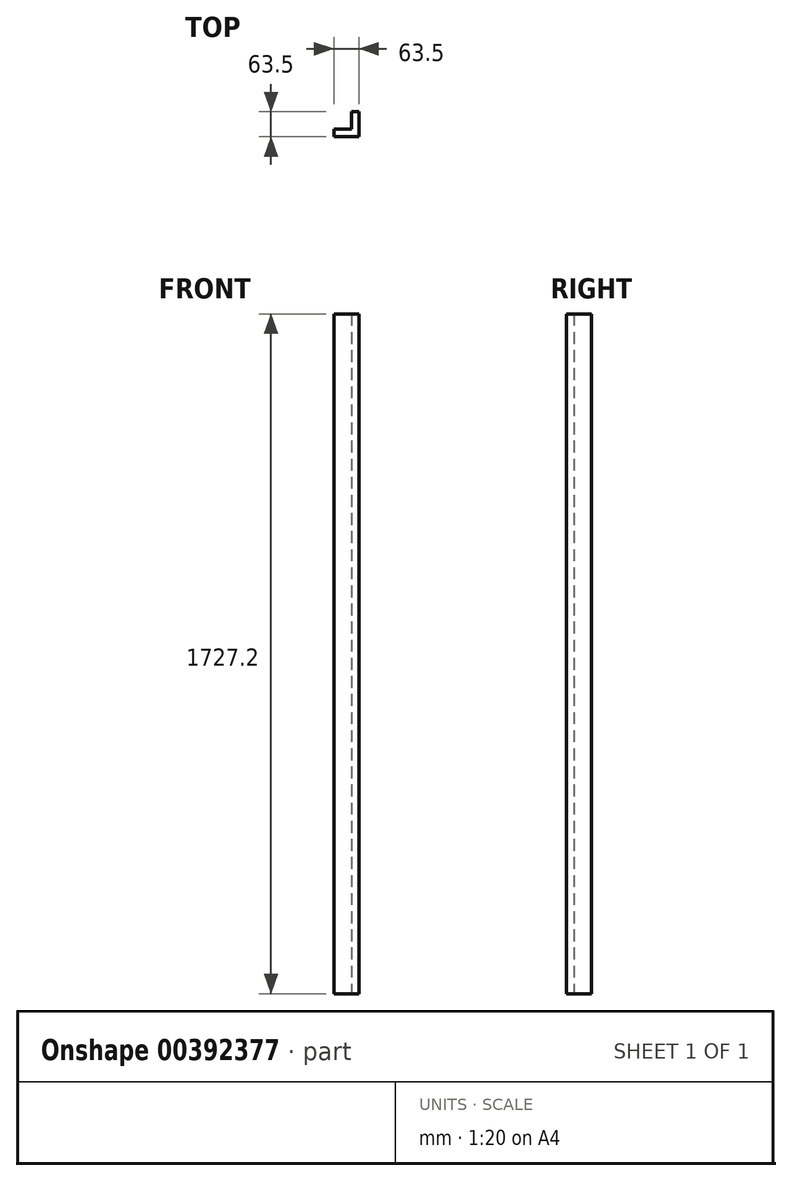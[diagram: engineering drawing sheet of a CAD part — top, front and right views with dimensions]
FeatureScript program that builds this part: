
annotation { "Feature Type Name" : "Feature", "Feature Type Description" : "" }
export const myFeature = defineFeature(function(context is Context, id is Id, definition is map)
    precondition{}
    {
        {
            var Q0;
            Q0=qCreatedBy(makeId("Top.planeOp"),FACE);
            var sketch = newSketch(context, id + "F0", { "sketchPlane" : qUnion([Q0])});
            skLineSegment(sketch, "E0", {"start": v(0, 0) * mm, "end": v(0, -63.5) * mm});
            skLineSegment(sketch, "E1", {"start": v(0, -63.5) * mm, "end": v(-63.5, -63.5) * mm});
            skLineSegment(sketch, "E2", {"start": v(-63.5, -63.5) * mm, "end": v(-63.5, -44.45) * mm});
            skLineSegment(sketch, "E3", {"start": v(-63.5, -44.45) * mm, "end": v(-19.05, -44.45) * mm});
            skLineSegment(sketch, "E4", {"start": v(-19.05, -44.45) * mm, "end": v(-19.05, 0) * mm});
            skLineSegment(sketch, "E5", {"start": v(-19.05, 0) * mm, "end": v(0, 0) * mm});
            skSolve(sketch);
        }
        {
            var Q0;
            Q0=makeQuery(id+"F0.imprint","IMPRINT",FACE,{"disambiguationData":[TD([[makeQuery(id+"F0.imprint","IMPRINT",EDGE,{"derivedFrom":sQuery(id+"F0.wireOp",EDGE,"E0")}),-1.0]])]});
            extrude(context, id + "F1", {"entities" : qUnion([Q0]), "depth" : 1727.2 * mm});
        }
    });
